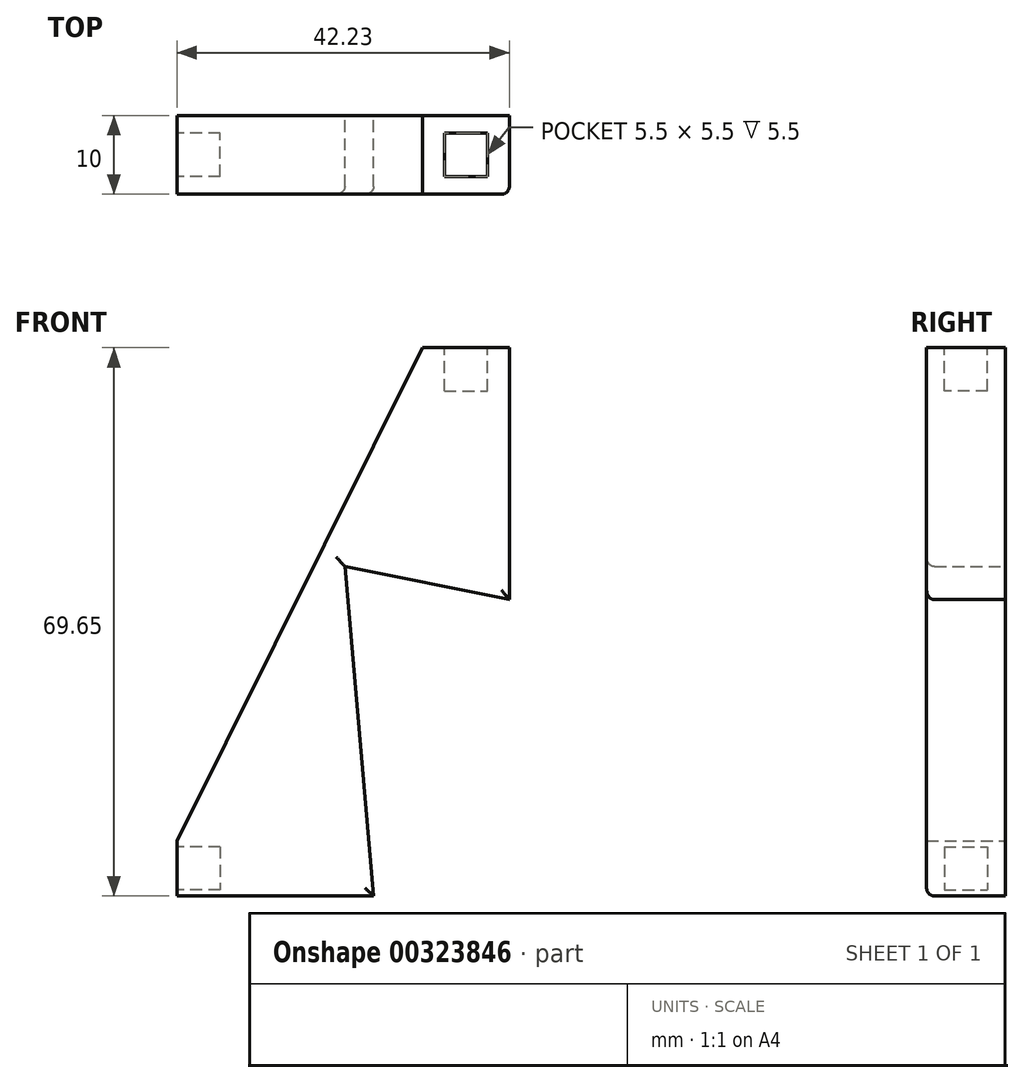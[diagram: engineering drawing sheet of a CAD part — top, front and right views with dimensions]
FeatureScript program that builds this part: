
annotation { "Feature Type Name" : "Feature", "Feature Type Description" : "" }
export const myFeature = defineFeature(function(context is Context, id is Id, definition is map)
    precondition{}
    {
        {
            var Q0;
            Q0=qCreatedBy(makeId("Front.planeOp"),FACE);
            var sketch = newSketch(context, id + "F0", { "sketchPlane" : qUnion([Q0])});
            skLineSegment(sketch, "E0", {"start": v(0, 0) * mm, "end": v(11, 0) * mm});
            skLineSegment(sketch, "E1", {"start": v(11, 0) * mm, "end": v(11, -32) * mm});
            skLineSegment(sketch, "E2", {"start": v(0, 0) * mm, "end": v(-31.23, -62.65) * mm});
            skLineSegment(sketch, "E3", {"start": v(-31.23, -62.65) * mm, "end": v(-31.23, -69.65) * mm});
            skLineSegment(sketch, "E4", {"start": v(-31.23, -69.65) * mm, "end": v(-6.23, -69.65) * mm});
            skLineSegment(sketch, "E5", {"start": v(-6.23, -69.65) * mm, "end": v(-9.9, -27.8) * mm});
            skLineSegment(sketch, "E6", {"start": v(-9.9, -27.8) * mm, "end": v(11, -32) * mm});
            skSolve(sketch);
        }
        {
            var Q0;
            Q0 = qSketchRegion(id + "F0", true);
            extrude(context, id + "F1", {"entities" : qUnion([Q0]), "depth" : 10 * mm});
        }
        {
            var Q0;
            Q0=makeQuery(id+"F1.opExtrude","SWEPT_FACE",FACE,{"disambiguationData":[OSD([sQuery(id+"F0.wireOp",EDGE,"E3")])]});
            var sketch = newSketch(context, id + "F2", { "sketchPlane" : qUnion([Q0])});
            skLineSegment(sketch, "E7", {"start": v(10, -63.4) * mm, "end": v(7.75, -63.4) * mm});
            skLineSegment(sketch, "E8", {"start": v(7.75, -63.4) * mm, "end": v(7.75, -62.65) * mm});
            skLineSegment(sketch, "E9.bottom", {"start": v(7.75, -63.4) * mm, "end": v(2.25, -63.4) * mm});
            skLineSegment(sketch, "E9.top", {"start": v(7.75, -68.9) * mm, "end": v(2.25, -68.9) * mm});
            skLineSegment(sketch, "E9.left", {"start": v(7.75, -63.4) * mm, "end": v(7.75, -68.9) * mm});
            skLineSegment(sketch, "E9.right", {"start": v(2.25, -63.4) * mm, "end": v(2.25, -68.9) * mm});
            skSolve(sketch);
        }
        {
            var Q0;
            Q0 = qSketchRegion(id + "F2", true);
            extrude(context, id + "F3", {"entities" : qUnion([Q0]), "operationType" : NewBodyOperationType.REMOVE, "oppositeDirection" : true, "depth" : 5.5 * mm});
        }
        {
            var Q0;
            Q0=makeQuery(id+"F1.opExtrude","SWEPT_FACE",FACE,{"disambiguationData":[OSD([sQuery(id+"F0.wireOp",EDGE,"E0")])]});
            var sketch = newSketch(context, id + "F4", { "sketchPlane" : qUnion([Q0])});
            skLineSegment(sketch, "E10", {"start": v(2.75, 0) * mm, "end": v(2.75, -2.25) * mm});
            skLineSegment(sketch, "E11", {"start": v(2.75, -2.25) * mm, "end": v(0, -2.25) * mm});
            skLineSegment(sketch, "E12.bottom", {"start": v(2.75, -2.25) * mm, "end": v(8.25, -2.25) * mm});
            skLineSegment(sketch, "E12.top", {"start": v(2.75, -7.75) * mm, "end": v(8.25, -7.75) * mm});
            skLineSegment(sketch, "E12.left", {"start": v(2.75, -2.25) * mm, "end": v(2.75, -7.75) * mm});
            skLineSegment(sketch, "E12.right", {"start": v(8.25, -2.25) * mm, "end": v(8.25, -7.75) * mm});
            skSolve(sketch);
        }
        {
            var Q0;
            Q0 = qSketchRegion(id + "F4", true);
            extrude(context, id + "F5", {"entities" : qUnion([Q0]), "operationType" : NewBodyOperationType.REMOVE, "oppositeDirection" : true, "depth" : 5.5 * mm});
        }
        {
            var Q0;
            Q0=makeQuery(id+"F1.opExtrude","CAP_EDGE",EDGE,{"disambiguationData":[OSD([sQuery(id+"F0.wireOp",EDGE,"E6")])],"isStart":false});
            var Q1;
            Q1=makeQuery(id+"F1.opExtrude","CAP_EDGE",EDGE,{"disambiguationData":[OSD([sQuery(id+"F0.wireOp",EDGE,"E4")])],"isStart":false});
            var Q2;
            Q2=makeQuery(id+"F1.opExtrude","CAP_EDGE",EDGE,{"disambiguationData":[OSD([sQuery(id+"F0.wireOp",EDGE,"E5")])],"isStart":false});
            var Q3;
            Q3=makeQuery(id+"F1.opExtrude","CAP_EDGE",EDGE,{"disambiguationData":[OSD([sQuery(id+"F0.wireOp",EDGE,"E1")])],"isStart":false});
            fillet(context, id + "F6", {"entities" : qUnion([Q0, Q1, Q2, Q3]), "radius" : 1 * mm, "tangentPropagation" : true, "allowEdgeOverflow" : false});
        }
    });
